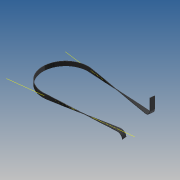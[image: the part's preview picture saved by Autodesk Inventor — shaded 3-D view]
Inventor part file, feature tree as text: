
AUTODESK INVENTOR PART (.ipt)
format: ipt  version: 2013 (Build 170138000, 138)  size: 166,400 bytes
history: native  units: mm
features: sketch x8, extrude x4, plane x3, other x2, helix x2, revolve x2, reference x2
ambient origin geometry x8: Origin, YZ Plane, XZ Plane, XY Plane, X Axis, Y Axis, Z Axis, Center Point
bodies: Solid1 (feature_tree)
feature tree (23):
  extrude  "Extrusion1"  Depth=0.254mm
  extrude  "Extrusion2"  Depth=6.0mm TaperAngle=0.0deg
  sketch  "Sketch3"  dims[d9=0.254mm]
  other  "Work Axis1"
  helix  "Coil1"  [1 undecoded]
  sketch  "Sketch4"  dims[d10=91.864mm d11=91.864mm d12=2.5mm d13=0.0mm d14=90.0deg d15=90.0deg d16=0.0mm d17=0.0mm d18=0.254mm]
  other  "Work Axis2"
  helix  "Coil2"  [1 undecoded]
  revolve  "Revolution1"  [1 undecoded]
  revolve  "Revolution2"  [1 undecoded]
  plane  "Work Plane1"
  plane  "Work Plane2"
  plane  "Work Plane3"
  extrude  "Extrusion4"  Depth=7.0mm
  extrude  "Extrusion5"  Depth=10.0mm TaperAngle=0.0deg
  sketch  "Sketch1"  dims[d0=63.661977mm d2=0.254mm]
  sketch  "Sketch2"  dims[d3=0.375mm d4=6.0mm d5=0.0mm d6=29.040533mm d7=0.0mm d8=0.0mm]
  sketch  "Sketch5"  dims[d19=91.864mm d20=91.864mm d21=2.5mm d22=0.0mm d23=90.0deg d24=90.0deg d25=0.0mm d26=0.0mm d27=7.0mm]
  sketch  "Sketch6"  dims[d28=90.0deg d29=7.0mm]
  sketch  "Sketch8"  dims[d30=90.0deg d34=10.0mm d35=0.0mm]
  reference  "Reference1"
  sketch  "Sketch9"  dims[d36=10.0mm d37=0.0mm]
  reference  "Reference2"
note: 4 required parameter values undecoded (feature->parameter linkage not recoverable at this tier; creation-order binding heuristic only, values carry confidence <= 0.55)